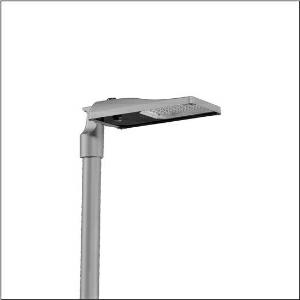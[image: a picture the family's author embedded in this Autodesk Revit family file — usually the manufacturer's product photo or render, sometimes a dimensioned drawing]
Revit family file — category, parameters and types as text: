
# Revit family: streetlight_sl_31_mini___st1_5a_5xh6p31t08ha_0610
name_source: partatom
category: Lighting Fixtures
units: mm (PartAtom-declared; Revit-internal decimal feet)

## family parameters
Cut with Voids When Loaded = No
Host = Face
Light Source = No
Part Type = Normal
Room Calculation Point = No
Round Connector Dimension = Use Diameter
Shared = No

## types (1)
- --- (1 x LED, 9070 lm, 68.3 W, 3000K)
    Apparent Load = 68 VA
    CIE Flux Codes = 22 53 95 100 100
    Color Rendering = 70
    Color Temperature = 3000K
    Default Elevation = 1800 mm
    Description = Streetlight SL 31 mini D4i, Desk-Remote mast luminaire for post-top, side-entry; light control with lens of PMMA; light distribution: ST1.5a, direct asymmetric distribution, for standard-compliant lighting for roads and squares; LED: luminous flux: 9.070lm, light colour: 730, colour temperature: 3000K; luminous efficacy: 132,8lm/W; control: pre-setting: logarithmic dimming characteristic, flexible luminous flux parameterisation, time-dependent luminous flux control, constant luminous flux control, power reduction, intelligent temperature release in ECG and LED module, overheat protection; luminaire housing, of diecast aluminium, Siteco® metallic grey (DB 702S), corrosivity category C5 high according to DIN EN ISO 12944; cover of toughened safety glass, transparent, opened without tools; mast flange of diecast aluminium, Siteco® metallic grey (DB 702S), spigot size: 76/60mm, mast flange included unmounted; with cable H07RN-F 2x 1.5mm², cable length: 8,5m, connection cable pre-assembled; mains connection: 220..240V, AC, 50/60Hz; power consumption (at start of service life): 68,3W / (at end of service life): 74,5W / (with reduced operation 50%): 29,5W; protection rating (complete): IP66; insulation class (complete): insulation class II (safety insulation); impact resistance: IK09; certification: CE, ENEC, ENEC+, VDE, UKCA, ZD4i; permissible operating ambient temperature for outdoor applications: -40..+50°C; packaging unit: 1 piece

Light Distribution: ST1.5a
    Height = 76 mm
    Lamp = 1 x LED
    Lamp Light Flux = 9070 lm
    Lamp Power = 68.3 W
    Lamp count = 1
    Length = 547 mm
    Luminous efficacy = 133 lm/W
    Manufacturer = Siteco
    ModVariant = No
    Model = 5XH6P31T08HA
    Number of Poles = 1
    OnlyDefault = Yes
    Power Factor = 1
    Product Name = Streetlight SL 31 mini | ST1.5a
    Product group = mast luminaire | pylon top
    ProductGroupID = 6100
    Protection Class = Protection class II
    Protection Degree = IP 66
    RLX_Detail_Level = 1
    RLX_Emergency_Light_Flux = 0 lm
    RLX_Emergency_Type = 0
    RLX_Emergency_Type_DB = No
    RlxData = <blob elided: 27849 chars, md5=7df38b0d>
    Socket = socket
    Standby Power = 0 W
    System Light Flux = 9070 lm
    System Power = 68 W
    Type Comments = factory setting: luminous flux: 100 % | dim-lin: 254 | 692 mA
    Type Image = l_1300332.jpg
    URL = http://relux.com
    VarID = @adj_003375
    Voltage = 0 V
    Weight = 0.00 kg
    Width = 265 mm

## geometry (parser evidence)
native form markers: Blend x4, Sweep x12
no freeform markers — native parametric forms only
